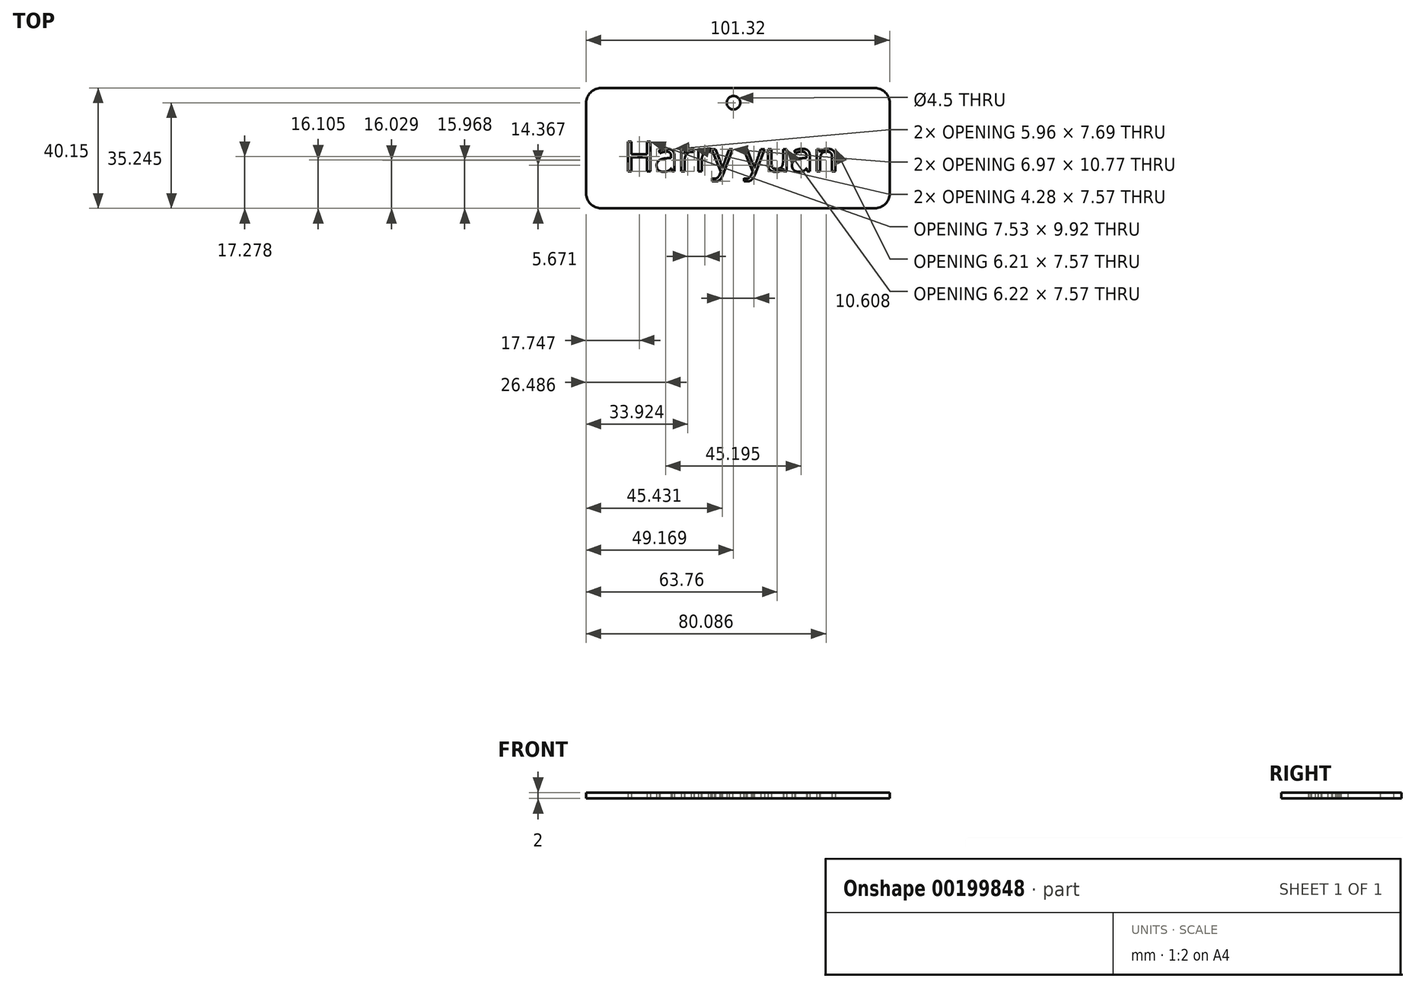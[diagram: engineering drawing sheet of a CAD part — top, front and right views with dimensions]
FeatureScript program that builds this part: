
annotation { "Feature Type Name" : "Feature", "Feature Type Description" : "" }
export const myFeature = defineFeature(function(context is Context, id is Id, definition is map)
    precondition{}
    {
        {
            var Q0;
            Q0=qCreatedBy(makeId("Top.planeOp"),FACE);
            var sketch = newSketch(context, id + "F0", { "sketchPlane" : qUnion([Q0])});
            skLineSegment(sketch, "E0.bottom", {"start": v(5, 0) * mm, "end": v(96.32, 0) * mm});
            skLineSegment(sketch, "E0.top", {"start": v(5, 40.15) * mm, "end": v(96.32, 40.15) * mm});
            skLineSegment(sketch, "E0.left", {"start": v(0, 5) * mm, "end": v(0, 35.15) * mm});
            skLineSegment(sketch, "E0.right", {"start": v(101.32, 5) * mm, "end": v(101.32, 35.15) * mm});
            skPoint(sketch, "E1.visualSharp", {"position": v(0, 40.15) * mm});
            skArc(sketch, "E1.filletArc", {"start": v(5, 40.15) * mm, "mid": v(1.46, 38.68) * mm, "end": v(0, 35.15) * mm});
            skPoint(sketch, "E2.visualSharp", {"position": v(0, 0) * mm});
            skArc(sketch, "E2.filletArc", {"start": v(0, 5) * mm, "mid": v(1.46, 1.46) * mm, "end": v(5, 0) * mm});
            skPoint(sketch, "E3.visualSharp", {"position": v(101.32, 0) * mm});
            skArc(sketch, "E3.filletArc", {"start": v(96.32, 0) * mm, "mid": v(99.86, 1.46) * mm, "end": v(101.32, 5) * mm});
            skPoint(sketch, "E4.visualSharp", {"position": v(101.32, 40.15) * mm});
            skArc(sketch, "E4.filletArc", {"start": v(101.32, 35.15) * mm, "mid": v(99.86, 38.68) * mm, "end": v(96.32, 40.15) * mm});
            skCircle(sketch, "E5", {"center": v(49.17, 35.25) * mm, "radius": 2.25 * mm});
            skText(sketch, "E6", { "text": "Harry yuan\n", "fontName": "OpenSans-Regular.ttf"});
            const initialGuessF0  = {"E6": [0.01262, 0.01232, 1, 0, 0.01]};
            skSetInitialGuess(sketch, initialGuessF0);
            skSolve(sketch);
        }
        {
            var Q0;
            Q0=makeQuery(id+"F0.imprint","IMPRINT",FACE,{"disambiguationData":[TD([[makeQuery(id+"F0.imprint","IMPRINT",EDGE,{"derivedFrom":sQuery(id+"F0.wireOp",EDGE,"E0.bottom")}),1.0]])]});
            extrude(context, id + "F1", {"entities" : qUnion([Q0]), "depth" : 2 * mm});
        }
    });
